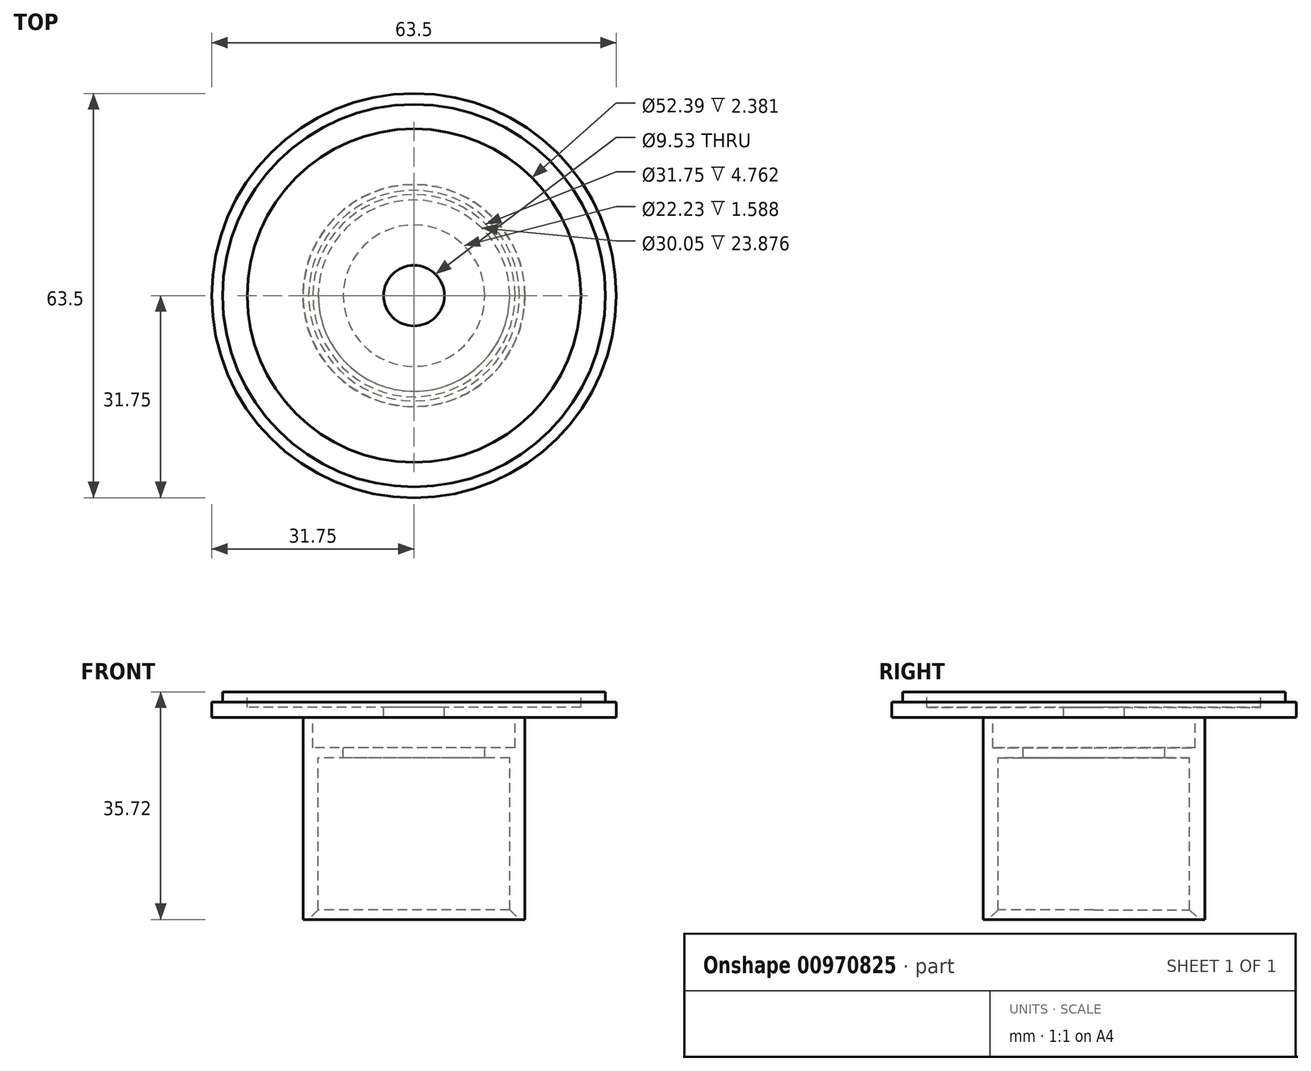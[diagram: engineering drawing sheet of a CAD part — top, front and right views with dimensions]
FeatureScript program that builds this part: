
annotation { "Feature Type Name" : "Feature", "Feature Type Description" : "" }
export const myFeature = defineFeature(function(context is Context, id is Id, definition is map)
    precondition{}
    {
        {
            var Q0;
            Q0=qCreatedBy(makeId("Front.planeOp"),FACE);
            var sketch = newSketch(context, id + "F0", { "sketchPlane" : qUnion([Q0])});
            skLineSegment(sketch, "E0", {"start": v(0, 0) * mm, "end": v(0, 53.06) * mm, "construction": true});
            skLineSegment(sketch, "E1", {"start": v(4.76, 0) * mm, "end": v(4.76, 1.59) * mm});
            skLineSegment(sketch, "E2", {"start": v(4.76, 0) * mm, "end": v(15.88, 0) * mm});
            skLineSegment(sketch, "E3", {"start": v(4.76, 1.59) * mm, "end": v(26.2, 1.59) * mm});
            skLineSegment(sketch, "E4", {"start": v(11.9, 14.1) * mm, "end": v(11.9, 12.52) * mm, "construction": true});
            skLineSegment(sketch, "E5.0", {"start": v(10.32, 16.08) * mm, "end": v(10.32, 12.52) * mm, "construction": true});
            skLineSegment(sketch, "E6", {"start": v(10.32, 12.52) * mm, "end": v(11.9, 12.52) * mm, "construction": true});
            skLineSegment(sketch, "E7.0", {"start": v(31.75, 11.32) * mm, "end": v(17.46, 14.5) * mm, "construction": true});
            skLineSegment(sketch, "E8", {"start": v(26.2, 3.97) * mm, "end": v(26.2, 1.59) * mm});
            skLineSegment(sketch, "E9", {"start": v(26.2, 3.97) * mm, "end": v(30.04, 3.97) * mm});
            skLineSegment(sketch, "E10", {"start": v(26.2, 10.93) * mm, "end": v(26.2, 8.73) * mm, "construction": true});
            skLineSegment(sketch, "E11", {"start": v(26.2, 8.73) * mm, "end": v(30.04, 8.73) * mm, "construction": true});
            skLineSegment(sketch, "E12.trimOffspring", {"start": v(26.2, 10.93) * mm, "end": v(11.9, 14.1) * mm, "construction": true});
            skLineSegment(sketch, "E13", {"start": v(15.88, 14.85) * mm, "end": v(15.88, 15.88) * mm, "construction": true});
            skLineSegment(sketch, "E14", {"start": v(15.88, 19.85) * mm, "end": v(11.11, 19.85) * mm, "construction": true});
            skLineSegment(sketch, "E15", {"start": v(11.11, 19.85) * mm, "end": v(11.11, 21.44) * mm, "construction": true});
            skLineSegment(sketch, "E16", {"start": v(17.46, 24.61) * mm, "end": v(17.46, 18.26) * mm, "construction": true});
            skLineSegment(sketch, "E17.trimOffspring", {"start": v(15.88, 14.85) * mm, "end": v(10.32, 16.08) * mm, "construction": true});
            skLineSegment(sketch, "E18", {"start": v(17.46, 24.61) * mm, "end": v(28.58, 24.61) * mm, "construction": true});
            skLineSegment(sketch, "E19", {"start": v(28.58, 24.61) * mm, "end": v(28.58, 27.79) * mm, "construction": true});
            skLineSegment(sketch, "E20", {"start": v(28.58, 27.79) * mm, "end": v(15.88, 27.79) * mm, "construction": true});
            skLineSegment(sketch, "E21", {"start": v(15.88, 27.79) * mm, "end": v(15.88, 21.44) * mm, "construction": true});
            skLineSegment(sketch, "E22", {"start": v(15.88, 21.44) * mm, "end": v(11.11, 21.44) * mm, "construction": true});
            skLineSegment(sketch, "E23", {"start": v(31.75, 11.32) * mm, "end": v(31.75, 10.32) * mm, "construction": true});
            skLineSegment(sketch, "E24", {"start": v(31.75, 2.38) * mm, "end": v(31.75, 0) * mm});
            skLineSegment(sketch, "E25", {"start": v(15.88, 0) * mm, "end": v(15.88, -4.76) * mm});
            skLineSegment(sketch, "E26", {"start": v(15.88, -4.76) * mm, "end": v(11.11, -4.76) * mm});
            skLineSegment(sketch, "E27", {"start": v(11.11, -4.76) * mm, "end": v(11.11, -6.35) * mm});
            skLineSegment(sketch, "E28.trimOffspring", {"start": v(17.46, 0) * mm, "end": v(31.75, 0) * mm});
            skLineSegment(sketch, "E29", {"start": v(11.11, -6.35) * mm, "end": v(15.02, -6.35) * mm});
            skLineSegment(sketch, "E30", {"start": v(15.02, -31.75) * mm, "end": v(17.4, -31.75) * mm});
            skLineSegment(sketch, "E31", {"start": v(15.02, -31.75) * mm, "end": v(15.02, -6.35) * mm});
            skLineSegment(sketch, "E32", {"start": v(17.4, 0) * mm, "end": v(17.4, -31.75) * mm});
            skLineSegment(sketch, "E33", {"start": v(15.87, 18.26) * mm, "end": v(17.46, 18.26) * mm, "construction": true});
            skLineSegment(sketch, "E34", {"start": v(15.87, 15.88) * mm, "end": v(17.46, 15.88) * mm, "construction": true});
            skLineSegment(sketch, "E35.trimOffspring", {"start": v(15.88, 18.26) * mm, "end": v(15.88, 19.85) * mm, "construction": true});
            skLineSegment(sketch, "E36.trimOffspring", {"start": v(17.46, 15.88) * mm, "end": v(17.46, 14.5) * mm, "construction": true});
            skLineSegment(sketch, "E37", {"start": v(31.75, 10.32) * mm, "end": v(30.04, 10.32) * mm, "construction": true});
            skLineSegment(sketch, "E38", {"start": v(30.04, 10.32) * mm, "end": v(30.04, 8.73) * mm, "construction": true});
            skLineSegment(sketch, "E39", {"start": v(31.75, 2.38) * mm, "end": v(30.04, 2.38) * mm});
            skLineSegment(sketch, "E40", {"start": v(30.04, 2.38) * mm, "end": v(30.04, 3.97) * mm});
            skSolve(sketch);
        }
        {
            var Q0;
            Q0 = qConstructionFilter(qBodyType(qCreatedBy(id + "F0" ,EDGE), BodyType.WIRE), ConstructionObject.NO);
            var Q1;
            Q1=sQuery(id+"F0.wireOp",EDGE,"E0");
            revolve(context, id + "F1", {"bodyType" : ToolBodyType.SURFACE, "surfaceOperationType" : NewSurfaceOperationType.NEW, "surfaceEntities" : qUnion([Q0]), "axis" : qUnion([Q1]), "revolveType" : RevolveType.FULL});
        }
        {
            var Q0;
            Q0=makeQuery(id+"F1.opRevolve","SWEPT_EDGE",EDGE,{"disambiguationData":[OSD([sQuery(id+"F0.wireOp",VERTEX,"E31.start")])]});
            chamfer(context, id + "F2", {"entities" : qUnion([Q0]), "width" : 1.52 * mm, "tangentPropagation" : true});
        }
    });
